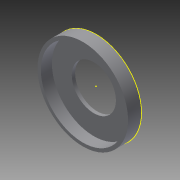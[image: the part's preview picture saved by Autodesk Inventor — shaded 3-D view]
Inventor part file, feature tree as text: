
AUTODESK INVENTOR PART (.ipt)
format: ipt  version: 2013 (Build 170138000, 138)  size: 105,472 bytes
history: native  units: mm
features: sketch x5, extrude x4, other x1
ambient origin geometry x8: Origin, YZ Plane, XZ Plane, XY Plane, X Axis, Y Axis, Z Axis, Center Point
feature tree (10):
  other  "ソリッド1"
  extrude  "押し出し1"  Depth=76.0mm
  extrude  "押し出し2"  Depth=82.0mm
  sketch  "スケッチ3"
  extrude  "押し出し3"  Depth=10.0mm TaperAngle=0.0deg
  extrude  "押し出し4"  Depth=2.0mm TaperAngle=0.0deg
  sketch  "スケッチ1"
  sketch  "スケッチ2"
  sketch  "スケッチ4"
  sketch  "スケッチ5"
